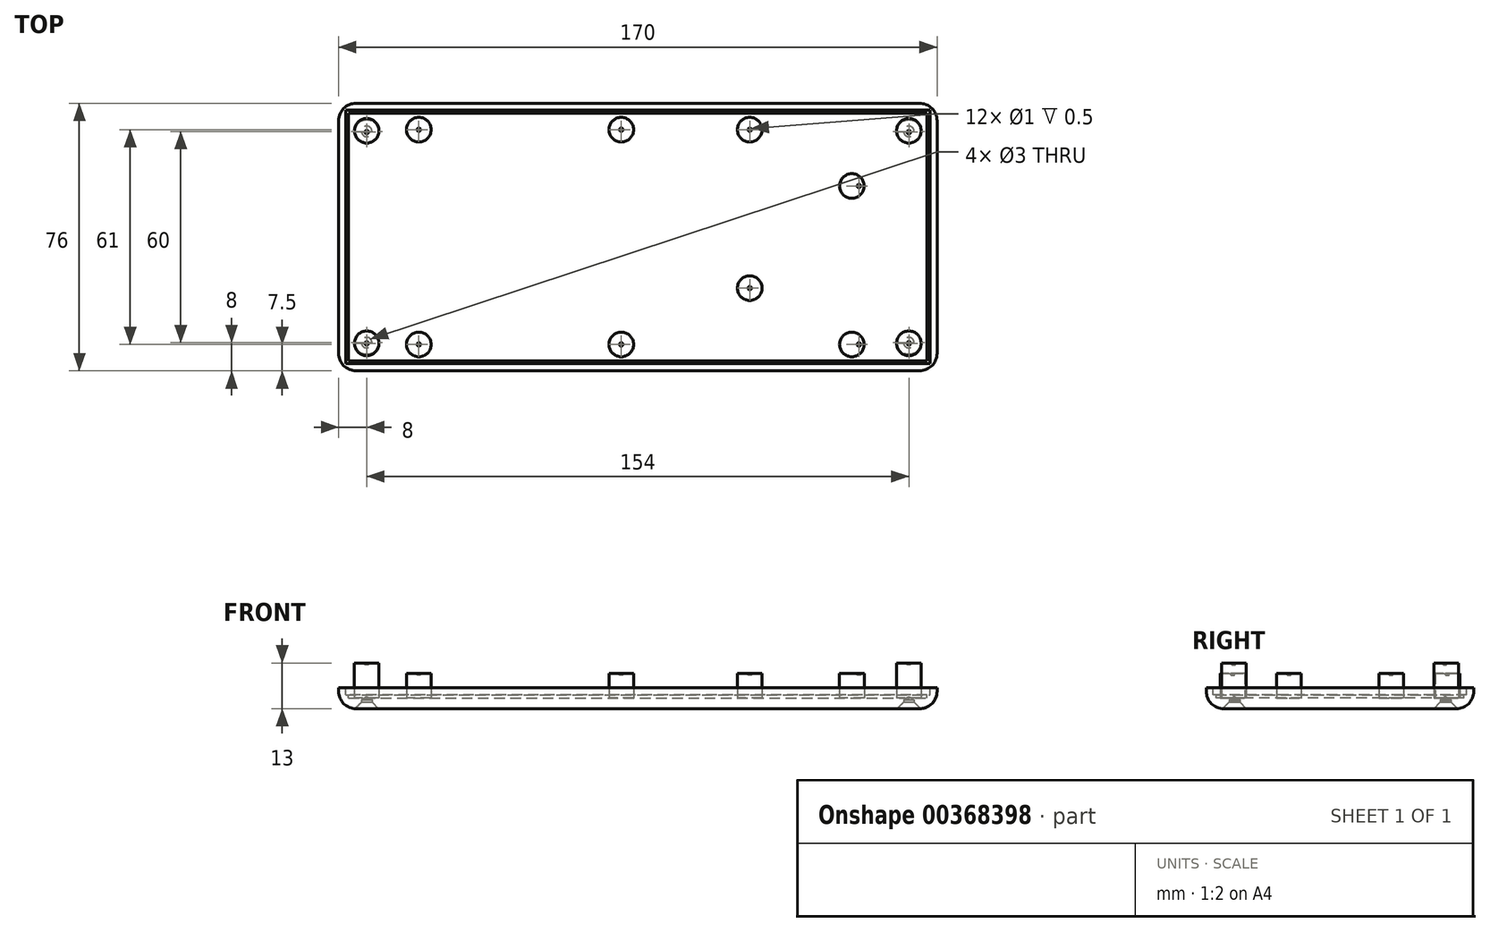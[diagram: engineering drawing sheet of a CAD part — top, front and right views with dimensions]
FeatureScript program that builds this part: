
annotation { "Feature Type Name" : "Feature", "Feature Type Description" : "" }
export const myFeature = defineFeature(function(context is Context, id is Id, definition is map)
    precondition{}
    {
        {
            var Q0;
            Q0=qCreatedBy(makeId("Top.planeOp"),FACE);
            var sketch = newSketch(context, id + "F0", { "sketchPlane" : qUnion([Q0])});
            skLineSegment(sketch, "E0.bottom", {"start": v(0, 0) * mm, "end": v(170, 0) * mm});
            skLineSegment(sketch, "E0.top", {"start": v(0, 76) * mm, "end": v(170, 76) * mm});
            skLineSegment(sketch, "E0.left", {"start": v(0, 0) * mm, "end": v(0, 76) * mm});
            skLineSegment(sketch, "E0.right", {"start": v(170, 0) * mm, "end": v(170, 76) * mm});
            skSolve(sketch);
        }
        {
            var Q0;
            Q0=qSketchRegion(id+"F0",true);
            extrude(context, id + "F1", {"entities" : qUnion([Q0]), "depth" : 6 * mm});
        }
        {
            var Q0;
            Q0=makeQuery(id+"F1.opExtrude","CAP_FACE",FACE,{"disambiguationData":[OSD([sQuery(id+"F0.wireOp",EDGE,"E0.bottom"),sQuery(id+"F0.wireOp",EDGE,"E0.top"),sQuery(id+"F0.wireOp",EDGE,"E0.left"),sQuery(id+"F0.wireOp",EDGE,"E0.right")])],"isStart":false});
            var sketch = newSketch(context, id + "F2", { "sketchPlane" : qUnion([Q0])});
            skLineSegment(sketch, "E1.bottom", {"start": v(2.8, 73.2) * mm, "end": v(167.2, 73.2) * mm});
            skLineSegment(sketch, "E1.top", {"start": v(2.8, 2.8) * mm, "end": v(167.2, 2.8) * mm});
            skLineSegment(sketch, "E1.left", {"start": v(2.8, 73.2) * mm, "end": v(2.8, 2.8) * mm});
            skLineSegment(sketch, "E1.right", {"start": v(167.2, 73.2) * mm, "end": v(167.2, 2.8) * mm});
            skSolve(sketch);
        }
        {
            var Q0;
            Q0=qSketchRegion(id+"F2",true);
            extrude(context, id + "F3", {"entities" : qUnion([Q0]), "operationType" : NewBodyOperationType.REMOVE, "oppositeDirection" : true, "depth" : 3 * mm});
        }
        {
            var Q0;
            Q0=makeQuery(id+"F3.boolean.opBoolean","COPY",FACE,{"derivedFrom":makeQuery(id+"F3.opExtrude","CAP_FACE",FACE,{"disambiguationData":[OSD([sQuery(id+"F2.wireOp",EDGE,"E1.bottom"),sQuery(id+"F2.wireOp",EDGE,"E1.top"),sQuery(id+"F2.wireOp",EDGE,"E1.left"),sQuery(id+"F2.wireOp",EDGE,"E1.right")])],"isStart":false})});
            var sketch = newSketch(context, id + "F4", { "sketchPlane" : qUnion([Q0])});
            skCircle(sketch, "E2", {"center": v(22.8, 68.5) * mm, "radius": 3.5 * mm});
            skCircle(sketch, "E3.0.1.0", {"center": v(22.8, 7.5) * mm, "radius": 3.5 * mm});
            skCircle(sketch, "E3.1.0.0", {"center": v(80.3, 68.5) * mm, "radius": 3.5 * mm});
            skCircle(sketch, "E3.1.1.0", {"center": v(80.3, 7.5) * mm, "radius": 3.5 * mm});
            skLineSegment(sketch, "E3.direction1", {"start": v(22.8, 68.5) * mm, "end": v(80.3, 68.5) * mm, "construction": true});
            skLineSegment(sketch, "E3.direction2", {"start": v(22.8, 68.5) * mm, "end": v(22.8, 7.5) * mm, "construction": true});
            skLineSegment(sketch, "E4", {"start": v(22.8, 38) * mm, "end": v(53.64, 38) * mm, "construction": true});
            skCircle(sketch, "E5", {"center": v(116.8, 68.5) * mm, "radius": 3.5 * mm});
            skCircle(sketch, "E6", {"center": v(145.8, 52.5) * mm, "radius": 3.5 * mm});
            skLineSegment(sketch, "E7", {"start": v(22.8, 7.5) * mm, "end": v(155.16, 7.5) * mm, "construction": true});
            skCircle(sketch, "E8.0.1.0", {"center": v(116.8, 23.5) * mm, "radius": 3.5 * mm});
            skCircle(sketch, "E8.0.1.1", {"center": v(145.8, 7.5) * mm, "radius": 3.5 * mm});
            skLineSegment(sketch, "E8.direction1", {"start": v(116.8, 68.5) * mm, "end": v(142, 68.5) * mm, "construction": true});
            skLineSegment(sketch, "E8.direction2", {"start": v(116.8, 68.5) * mm, "end": v(116.8, 23.5) * mm, "construction": true});
            skLineSegment(sketch, "E9", {"start": v(2.8, 38) * mm, "end": v(167.2, 38) * mm, "construction": true});
            skLineSegment(sketch, "E10.MirrorCS", {"start": v(168.2, 38) * mm, "end": v(11.2, 38) * mm, "construction": true});
            skSolve(sketch);
        }
        {
            var Q0;
            Q0=qSketchRegion(id+"F4",true);
            extrude(context, id + "F5", {"entities" : qUnion([Q0]), "operationType" : NewBodyOperationType.ADD, "depth" : 7 * mm});
        }
        {
            var Q0;
            Q0=makeQuery(id+"F1.opExtrude","SWEPT_FACE",FACE,{"disambiguationData":[OSD([sQuery(id+"F0.wireOp",EDGE,"E0.left")])]});
            var sketch = newSketch(context, id + "F6", { "sketchPlane" : qUnion([Q0])});
            skCircle(sketch, "E11", {"center": v(-57, 18) * mm, "radius": 4 * mm});
            skLineSegment(sketch, "E12", {"start": v(-38, 6) * mm, "end": v(-38, 0) * mm, "construction": true});
            skCircle(sketch, "E13.MirrorC", {"center": v(-19, 18) * mm, "radius": 4 * mm});
            skSolve(sketch);
        }
        {
            var Q0;
            Q0=qSketchRegion(id+"F6",true);
            var Q1;
            Q1=makeQuery(id+"F3.boolean.opBoolean","COPY",FACE,{"derivedFrom":makeQuery(id+"F3.opExtrude","SWEPT_FACE",FACE,{"disambiguationData":[OSD([sQuery(id+"F2.wireOp",EDGE,"E1.left")])]})});
            extrude(context, id + "F7", {"entities" : qUnion([Q0]), "operationType" : NewBodyOperationType.REMOVE, "endBound" : BoundingType.UP_TO_SURFACE, "oppositeDirection" : true, "endBoundEntityFace" : qUnion([Q1]), "depth" : 25 * mm});
        }
        {
            var Q0;
            {var subQ0=sQuery(id+"F0.wireOp",EDGE,"E0.left");var subQ1=sQuery(id+"F0.wireOp",EDGE,"E0.top");var subQ2=sQuery(id+"F0.wireOp",EDGE,"E0.right");var subQ3=sQuery(id+"F0.wireOp",EDGE,"E0.bottom");Q0=makeQuery(id+"F7.boolean.opBoolean","SPLIT",FACE,{"disambiguationData":[TD([makeQuery(id+"F1.opExtrude","SWEPT_FACE",FACE,{"disambiguationData":[OSD([subQ3])]}),makeQuery(id+"F1.opExtrude","SWEPT_FACE",FACE,{"disambiguationData":[OSD([subQ1])]}),makeQuery(id+"F1.opExtrude","SWEPT_FACE",FACE,{"disambiguationData":[OSD([subQ0])]}),makeQuery(id+"F1.opExtrude","SWEPT_FACE",FACE,{"disambiguationData":[OSD([subQ2])]}),makeQuery(id+"F3.boolean.opBoolean","COPY",FACE,{"derivedFrom":makeQuery(id+"F3.opExtrude","SWEPT_FACE",FACE,{"disambiguationData":[OSD([sQuery(id+"F2.wireOp",EDGE,"E1.bottom")])]})}),makeQuery(id+"F3.boolean.opBoolean","COPY",FACE,{"derivedFrom":makeQuery(id+"F3.opExtrude","SWEPT_FACE",FACE,{"disambiguationData":[OSD([sQuery(id+"F2.wireOp",EDGE,"E1.top")])]})}),makeQuery(id+"F3.boolean.opBoolean","COPY",FACE,{"derivedFrom":makeQuery(id+"F3.opExtrude","SWEPT_FACE",FACE,{"disambiguationData":[OSD([sQuery(id+"F2.wireOp",EDGE,"E1.left")])]})}),makeQuery(id+"F3.boolean.opBoolean","COPY",FACE,{"derivedFrom":makeQuery(id+"F3.opExtrude","SWEPT_FACE",FACE,{"disambiguationData":[OSD([sQuery(id+"F2.wireOp",EDGE,"E1.right")])]})}),makeQuery(id+"F7.opExtrude","SWEPT_FACE",FACE,{"disambiguationData":[OSD([sQuery(id+"F6.wireOp",EDGE,"E11")])]}),makeQuery(id+"F7.opExtrude","SWEPT_FACE",FACE,{"disambiguationData":[OSD([sQuery(id+"F6.wireOp",EDGE,"E13.MirrorC")])]})])],"derivedFrom":makeQuery(id+"F1.opExtrude","CAP_FACE",FACE,{"disambiguationData":[OSD([subQ3,subQ1,subQ0,subQ2])],"isStart":false})});}
            var sketch = newSketch(context, id + "F8", { "sketchPlane" : qUnion([Q0])});
            skLineSegment(sketch, "E14.bottom", {"start": v(2, 74) * mm, "end": v(168, 74) * mm});
            skLineSegment(sketch, "E14.top", {"start": v(2, 2) * mm, "end": v(168, 2) * mm});
            skLineSegment(sketch, "E14.left", {"start": v(2, 74) * mm, "end": v(2, 2) * mm});
            skLineSegment(sketch, "E14.right", {"start": v(168, 74) * mm, "end": v(168, 2) * mm});
            skLineSegment(sketch, "E15.bottom", {"start": v(3, 72.2) * mm, "end": v(166.2, 72.2) * mm});
            skLineSegment(sketch, "E15.top", {"start": v(3, 3) * mm, "end": v(166.2, 3) * mm});
            skLineSegment(sketch, "E15.left", {"start": v(3, 72.2) * mm, "end": v(3, 3) * mm});
            skLineSegment(sketch, "E15.right", {"start": v(166.2, 72.2) * mm, "end": v(166.2, 3) * mm});
            skSolve(sketch);
        }
        {
            var Q0;
            Q0=qSketchRegion(id+"F8",true);
            extrude(context, id + "F9", {"entities" : qUnion([Q0]), "operationType" : NewBodyOperationType.REMOVE, "oppositeDirection" : true, "depth" : 2 * mm});
        }
        {
            var Q0;
            Q0=makeQuery(id+"F4.imprint","IMPRINT",FACE,{"disambiguationData":[TD([[makeQuery(id+"F4.imprint","IMPRINT",EDGE,{"derivedFrom":sQuery(id+"F4.wireOp",EDGE,"E2")}),-1.0]])]});
            var sketch = newSketch(context, id + "F10", { "sketchPlane" : qUnion([Q0])});
            skCircle(sketch, "E16", {"center": v(8, 68.2) * mm, "radius": 3.5 * mm});
            skCircle(sketch, "E17.MirrorC", {"center": v(8, 7.8) * mm, "radius": 3.5 * mm});
            skCircle(sketch, "E18.1.0.0", {"center": v(162, 7.8) * mm, "radius": 3.5 * mm});
            skCircle(sketch, "E18.1.0.1", {"center": v(162, 68.2) * mm, "radius": 3.5 * mm});
            skLineSegment(sketch, "E18.direction1", {"start": v(8, 7.8) * mm, "end": v(162, 7.8) * mm, "construction": true});
            skSolve(sketch);
        }
        {
            var Q0;
            Q0=qSketchRegion(id+"F10",true);
            extrude(context, id + "F11", {"entities" : qUnion([Q0]), "operationType" : NewBodyOperationType.ADD, "depth" : 10 * mm});
        }
        {
            var Q0;
            Q0=makeQuery(id+"F11.opExtrude","CAP_FACE",FACE,{"disambiguationData":[OSD([sQuery(id+"F10.wireOp",EDGE,"E16")])],"isStart":false});
            var sketch = newSketch(context, id + "F12", { "sketchPlane" : qUnion([Q0])});
            skCircle(sketch, "E19", {"center": v(8, 67.8) * mm, "radius": 0.5 * mm});
            skCircle(sketch, "E20.MirrorC", {"center": v(8, 7.8) * mm, "radius": 0.5 * mm});
            skCircle(sketch, "E21.1.0.0", {"center": v(162, 7.8) * mm, "radius": 0.5 * mm});
            skCircle(sketch, "E21.1.0.1", {"center": v(162, 67.8) * mm, "radius": 0.5 * mm});
            skLineSegment(sketch, "E21.direction1", {"start": v(8, 7.8) * mm, "end": v(162, 7.8) * mm, "construction": true});
            skSolve(sketch);
        }
        {
            var Q0;
            Q0=qSketchRegion(id+"F12",true);
            extrude(context, id + "F13", {"entities" : qUnion([Q0]), "operationType" : NewBodyOperationType.REMOVE, "oppositeDirection" : true, "depth" : 0.5 * mm});
        }
        {
            var Q0;
            Q0=makeQuery(id+"F5.opExtrude","CAP_FACE",FACE,{"disambiguationData":[OSD([sQuery(id+"F4.wireOp",EDGE,"E2")])],"isStart":false});
            var sketch = newSketch(context, id + "F14", { "sketchPlane" : qUnion([Q0])});
            skCircle(sketch, "E22", {"center": v(22.8, 68.5) * mm, "radius": 0.5 * mm});
            skCircle(sketch, "E23.0.1.0", {"center": v(22.8, 7.5) * mm, "radius": 0.5 * mm});
            skCircle(sketch, "E23.1.0.0", {"center": v(80.3, 68.5) * mm, "radius": 0.5 * mm});
            skCircle(sketch, "E23.1.1.0", {"center": v(80.3, 7.5) * mm, "radius": 0.5 * mm});
            skLineSegment(sketch, "E23.direction1", {"start": v(22.8, 68.5) * mm, "end": v(80.3, 68.5) * mm, "construction": true});
            skLineSegment(sketch, "E23.direction2", {"start": v(22.8, 68.5) * mm, "end": v(22.8, 7.5) * mm, "construction": true});
            skLineSegment(sketch, "E24", {"start": v(22.8, 38) * mm, "end": v(53.44, 38) * mm, "construction": true});
            skCircle(sketch, "E25", {"center": v(116.8, 68.5) * mm, "radius": 0.5 * mm});
            skCircle(sketch, "E26", {"center": v(147.8, 52.5) * mm, "radius": 0.5 * mm});
            skLineSegment(sketch, "E27", {"start": v(22.8, 7.5) * mm, "end": v(131.04, 7.5) * mm, "construction": true});
            skCircle(sketch, "E28.0.1.0", {"center": v(116.8, 23.5) * mm, "radius": 0.5 * mm});
            skCircle(sketch, "E28.0.1.1", {"center": v(147.8, 7.5) * mm, "radius": 0.5 * mm});
            skLineSegment(sketch, "E28.direction1", {"start": v(116.8, 68.5) * mm, "end": v(117.88, 68.5) * mm, "construction": true});
            skLineSegment(sketch, "E28.direction2", {"start": v(116.8, 68.5) * mm, "end": v(116.8, 23.5) * mm, "construction": true});
            skLineSegment(sketch, "E29", {"start": v(-21.12, 79.96) * mm, "end": v(142.88, 79.96) * mm, "construction": true});
            skLineSegment(sketch, "E30.MirrorCS", {"start": v(144.08, 79.96) * mm, "end": v(-12.92, 79.96) * mm, "construction": true});
            skSolve(sketch);
        }
        {
            var Q0;
            Q0=qSketchRegion(id+"F14",true);
            extrude(context, id + "F15", {"entities" : qUnion([Q0]), "operationType" : NewBodyOperationType.REMOVE, "oppositeDirection" : true, "depth" : 0.5 * mm});
        }
        {
            var Q0;
            Q0=makeQuery(id+"F1.opExtrude","CAP_FACE",FACE,{"disambiguationData":[OSD([sQuery(id+"F0.wireOp",EDGE,"E0.bottom"),sQuery(id+"F0.wireOp",EDGE,"E0.top"),sQuery(id+"F0.wireOp",EDGE,"E0.left"),sQuery(id+"F0.wireOp",EDGE,"E0.right")])],"isStart":true});
            var sketch = newSketch(context, id + "F16", { "sketchPlane" : qUnion([Q0])});
            skCircle(sketch, "E31", {"center": v(8, -8) * mm, "radius": 2.5 * mm});
            skCircle(sketch, "E32.MirrorC", {"center": v(8, -68) * mm, "radius": 2.5 * mm});
            skCircle(sketch, "E33.1.0.0", {"center": v(162, -68) * mm, "radius": 2.5 * mm});
            skCircle(sketch, "E33.1.0.1", {"center": v(162, -8) * mm, "radius": 2.5 * mm});
            skLineSegment(sketch, "E33.direction1", {"start": v(8, -68) * mm, "end": v(162, -68) * mm, "construction": true});
            skSolve(sketch);
        }
        {
            var Q0;
            Q0=sQuery(id+"F16.wireOp",VERTEX,"E31.center");
            var Q1;
            Q1=sQuery(id+"F16.wireOp",VERTEX,"E32.MirrorC.center");
            var Q2;
            Q2=sQuery(id+"F16.wireOp",VERTEX,"E33.1.0.0.center");
            var Q3;
            Q3=sQuery(id+"F16.wireOp",VERTEX,"E33.1.0.1.center");
            var Q4;
            Q4=makeQuery(id+"F1.opExtrude","SWEPT_BODY",BODY,{"disambiguationData":[OSD([sQuery(id+"F0.wireOp",EDGE,"E0.bottom"),sQuery(id+"F0.wireOp",EDGE,"E0.top"),sQuery(id+"F0.wireOp",EDGE,"E0.left"),sQuery(id+"F0.wireOp",EDGE,"E0.right")])]});
            hole(context, id + "F17", {"style" : HoleStyle.C_SINK, "endStyle" : HoleEndStyle.BLIND, "holeDiameter" : 3 * mm, "cSinkDiameter" : 6.72 * mm, "cSinkAngle" : 90 * degree, "holeDepth" : 2.5 * mm, "isTappedThrough" : true, "tappedDepth" : 12 * mm, "tapClearance" : 3, "locations" : qUnion([Q0, Q1, Q2, Q3]), "scope" : qUnion([Q4])});
        }
        {
            var Q0;
            Q0=makeQuery(id+"F1.opExtrude","SWEPT_EDGE",EDGE,{"disambiguationData":[OSD([sQuery(id+"F0.wireOp",EDGE,"E0.top"),sQuery(id+"F0.wireOp",EDGE,"E0.right")])]});
            var Q1;
            Q1=makeQuery(id+"F1.opExtrude","SWEPT_EDGE",EDGE,{"disambiguationData":[OSD([sQuery(id+"F0.wireOp",EDGE,"E0.bottom"),sQuery(id+"F0.wireOp",EDGE,"E0.right")])]});
            var Q2;
            Q2=makeQuery(id+"F1.opExtrude","CAP_EDGE",EDGE,{"disambiguationData":[OSD([sQuery(id+"F0.wireOp",EDGE,"E0.right")])],"isStart":true});
            var Q3;
            Q3=makeQuery(id+"F1.opExtrude","CAP_EDGE",EDGE,{"disambiguationData":[OSD([sQuery(id+"F0.wireOp",EDGE,"E0.top")])],"isStart":true});
            var Q4;
            Q4=makeQuery(id+"F1.opExtrude","SWEPT_EDGE",EDGE,{"disambiguationData":[OSD([sQuery(id+"F0.wireOp",EDGE,"E0.top"),sQuery(id+"F0.wireOp",EDGE,"E0.left")])]});
            var Q5;
            Q5=makeQuery(id+"F1.opExtrude","CAP_EDGE",EDGE,{"disambiguationData":[OSD([sQuery(id+"F0.wireOp",EDGE,"E0.left")])],"isStart":true});
            var Q6;
            Q6=makeQuery(id+"F1.opExtrude","SWEPT_EDGE",EDGE,{"disambiguationData":[OSD([sQuery(id+"F0.wireOp",EDGE,"E0.bottom"),sQuery(id+"F0.wireOp",EDGE,"E0.left")])]});
            var Q7;
            Q7=makeQuery(id+"F1.opExtrude","CAP_EDGE",EDGE,{"disambiguationData":[OSD([sQuery(id+"F0.wireOp",EDGE,"E0.bottom")])],"isStart":true});
            fillet(context, id + "F18", {"entities" : qUnion([Q0, Q1, Q2, Q3, Q4, Q5, Q6, Q7]), "radius" : 5 * mm, "tangentPropagation" : true, "allowEdgeOverflow" : false});
        }
    });
